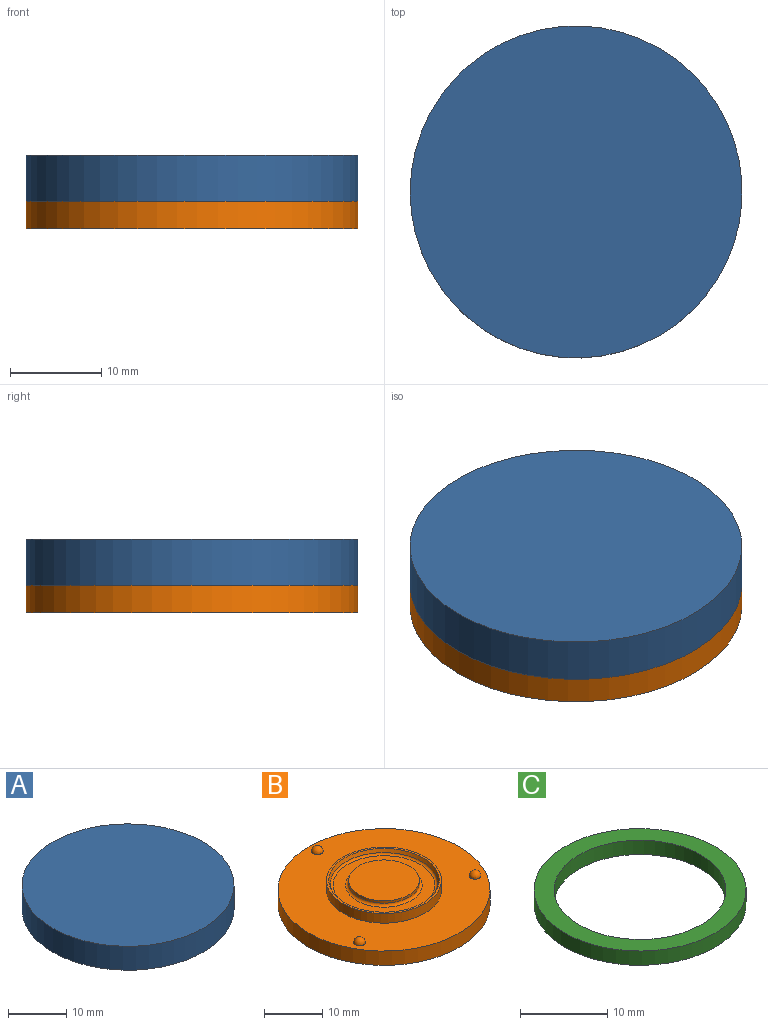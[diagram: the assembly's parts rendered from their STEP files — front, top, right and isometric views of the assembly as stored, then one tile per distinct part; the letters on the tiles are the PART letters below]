
ASSEMBLY  parts=3 mates=2
PART A: 14 faces, bbox 36.3x36.3x5 mm
  f0: sphere r=1.1mm, area 7.6mm2, adj f5
  f1: sphere r=1.1mm, area 7.6mm2, adj f5
  f2: plane 24.3x24.3mm, normal (0,0,-1), area 463.8mm2, adj f10
  f3: plane 36.3x36.3mm, normal (0,0,1), area 1034.9mm2, adj f4
  f4: cylinder r=18.15mm len=36.3mm, axis (0,0,-1), area 570.2mm2, adj f3,f5
  f5: plane 36.3x36.3mm, normal (0,0,-1), area 367.5mm2, adj f0,f1,f4,f6,f11
  f6: cylinder r=14.45mm len=28.9mm, axis (0,0,-1), area 45.4mm2, adj f5,f12
  f7: plane 27.9x27.9mm, normal (0,0,-1), area 56.6mm2, adj f12,f13
  f8: cone r=12.55mm half-angle=21.8deg, axis (0,0,1), area 58.9mm2, adj f9,f13
  f9: plane 25.1x25.1mm, normal (0,0,-1), area 31mm2, adj f8,f10
  f10: cylinder r=12.15mm len=24.3mm, axis (0,0,-1), area 152.7mm2, adj f2,f9
  f11: sphere r=1.1mm, area 7.6mm2, adj f5
  f12: torus R=13.95mm, axis (0,0,-1), area 70.4mm2, adj f6,f7
  f13: torus R=13.29mm, axis (0,0,-1), area 48.7mm2, adj f7,f8
PART B: 14 faces, bbox 36.3x36.3x5 mm
  f0: sphere r=1mm, area 6.3mm2, adj f2
  f1: sphere r=1mm, area 6.3mm2, adj f2
  f2: plane 36.3x36.3mm, normal (0,0,1), area 720.7mm2, adj f0,f1,f3,f10,f11
  f3: cylinder r=18.15mm len=36.3mm, axis (0,0,-1), area 342.1mm2, adj f2,f4
  f4: plane 36.3x36.3mm, normal (0,0,-1), area 1034.9mm2, adj f3
  f5: plane 12.1x12.1mm, normal (0,0,1), area 115mm2, adj f6
  f6: cylinder r=6.05mm len=12.1mm, axis (0,0,-1), area 19mm2, adj f5,f12
  f7: plane 17.42x17.42mm, normal (0,0,1), area 103.6mm2, adj f12,f13
  f8: cone r=9.45mm half-angle=21.8deg, axis (0,0,1), area 43.2mm2, adj f9,f13
  f9: plane 19.7x19.7mm, normal (0,0,1), area 24.3mm2, adj f8,f10
  f10: cylinder r=9.85mm len=19.7mm, axis (0,0,-1), area 123.8mm2, adj f2,f9
  f11: sphere r=1mm, area 6.3mm2, adj f2
  f12: torus R=6.55mm, axis (0,0,1), area 30.8mm2, adj f6,f7
  f13: torus R=8.71mm, axis (0,0,1), area 33.6mm2, adj f7,f8
PART C: 4 faces, bbox 24.3x24.3x2 mm
  f0: cylinder r=9.85mm len=19.7mm, axis (0,0,-1), area 123.8mm2, adj f2,f3
  f1: cylinder r=12.15mm len=24.3mm, axis (0,0,-1), area 152.7mm2, adj f2,f3
  f2: plane 24.3x24.3mm, normal (0,0,1), area 159mm2, adj f0,f1
  f3: plane 24.3x24.3mm, normal (0,0,-1), area 159mm2, adj f0,f1
PLACE A t=(0,0,-2)mm
PLACE B t=(0,0,-2)mm
PLACE C rot(axis=(1,0,0),180deg) t=(0,0,0)mm
MATE fastened B.f3 <-> A.f4  axis (0,0,1) through (0,0,0)mm
MATE fastened C.f0 <-> B.f3  axis (0,0,1) through (0,0,0)mm
